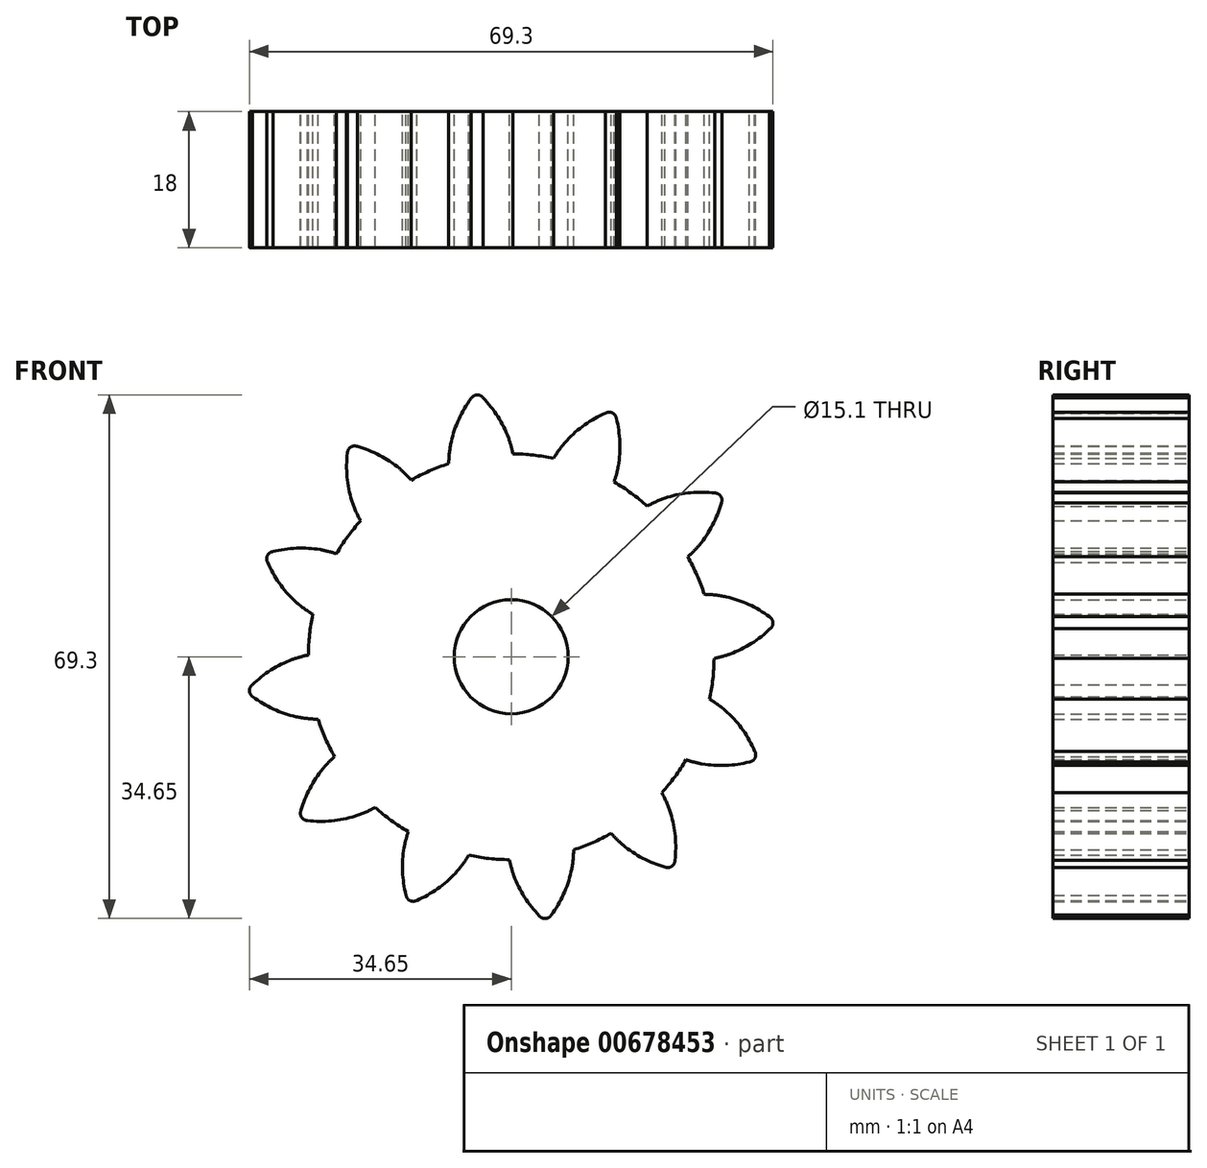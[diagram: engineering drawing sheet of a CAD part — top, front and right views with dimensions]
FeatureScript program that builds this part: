
annotation { "Feature Type Name" : "Feature", "Feature Type Description" : "" }
export const myFeature = defineFeature(function(context is Context, id is Id, definition is map)
    precondition{}
    {
        {
            var Q0;
            Q0=qCreatedBy(makeId("Front.planeOp"),FACE);
            var sketch = newSketch(context, id + "F0", { "sketchPlane" : qUnion([Q0])});
            skCircle(sketch, "E0", {"center": v(0, 0) * mm, "radius": 31.75 * mm, "construction": true});
            skCircle(sketch, "E1", {"center": v(0, 0) * mm, "radius": 29.34 * mm, "construction": true});
            skCircle(sketch, "E2", {"center": v(0, 0) * mm, "radius": 26.86 * mm});
            skArc(sketch, "E3", {"start": v(-0.36, 28.97) * mm, "mid": v(-1.76, 31.8) * mm, "end": v(-3.72, 34.29) * mm});
            skArc(sketch, "E4", {"start": v(0.51, 24) * mm, "mid": v(0.29, 26.53) * mm, "end": v(-0.36, 28.97) * mm});
            skArc(sketch, "E5.MirrorCS", {"start": v(-7.93, 28.48) * mm, "mid": v(-6.92, 31.47) * mm, "end": v(-5.3, 34.18) * mm});
            skArc(sketch, "E6.MirrorCS", {"start": v(-8.15, 23.44) * mm, "mid": v(-8.26, 25.97) * mm, "end": v(-7.93, 28.48) * mm});
            skArc(sketch, "E7", {"start": v(-3.72, 34.29) * mm, "mid": v(-4.54, 34.65) * mm, "end": v(-5.3, 34.18) * mm});
            skCircle(sketch, "E8", {"center": v(0, 0) * mm, "radius": 7.55 * mm});
            skSolve(sketch);
        }
        {
            var Q0;
            Q0=makeQuery(id+"F0.imprint","IMPRINT",FACE,{"disambiguationData":[TD([[makeQuery(id+"F0.imprint","IMPRINT",EDGE,{"derivedFrom":sQuery(id+"F0.wireOp",EDGE,"E2")}),1.0]])]});
            var Q1;
            {var subQ2=sQuery(id+"F0.wireOp",EDGE,"E3");Q1=makeQuery(id+"F0.imprint","IMPRINT",FACE,{"disambiguationData":[TD([[makeQuery(id+"F0.imprint","IMPRINT",EDGE,{"derivedFrom":subQ2}),1.0]])]});}
            extrude(context, id + "F1", {"entities" : qUnion([Q0, Q1]), "depth" : 18 * mm, "offsetDistance" : 25 * mm});
        }
        {
            var Q0;
            Q0=makeQuery(id+"F1.opExtrude","SWEPT_BODY",BODY,{"disambiguationData":[OSD([sQuery(id+"F0.wireOp",EDGE,"E2"),sQuery(id+"F0.wireOp",EDGE,"E3"),sQuery(id+"F0.wireOp",EDGE,"E4"),sQuery(id+"F0.wireOp",EDGE,"E5.MirrorCS"),sQuery(id+"F0.wireOp",EDGE,"E6.MirrorCS"),sQuery(id+"F0.wireOp",EDGE,"E7")])]});
            var Q1;
            Q1=makeQuery(id+"F1.opExtrude","SWEPT_FACE",FACE,{"disambiguationData":[OSD([sQuery(id+"F0.wireOp",EDGE,"E2")])]});
            circularPattern(context, id + "F2", {"operationType" : NewBodyOperationType.ADD, "entities" : qUnion([Q0]), "axis" : qUnion([Q1]), "angle" : 360 * degree, "instanceCount" : 12, "equalSpace" : true});
        }
    });
